# Revit family: DAC-H
name_source: partatom
category: Air Terminals
revit_build: Autodesk Revit MEP 2012 (Build: 20110309_2315(x64)
units: mm (PartAtom-declared; Revit-internal decimal feet)

## types (10) — shared parameters
Manufacturer = INNES
Max Flow = 0 CFM
Min Flow = 0 CFM
Máxima presión estática = 0.00 in-wg
Máxima velocidad de cuello = 0 FPM
Mínima presión estática = 0.00 in-wg
Mínima velocidad de cuello = 0 FPM
URL = http://www.innes.com.mx

## per-type parameters (varying)
| type | A | Ancho perfil medio | B | C | Cuello | Deflector | Largo frente | Largo perfil | Material | Medida req. | Máximo nivel de ruido (NC) | Perfil central | Soportes |
| DAC-I-01-3 | 3" | 1 31/32" | 5 3/4" | 4 11/16" |  | Yes | 146 7/8" | 143 15/16" |  | 144" |  | No | Yes |
| DAC-I-01-1 | 1" | 1 31/32" | 3 3/4" | 2 11/16" | Cuadrado | Yes | 26 7/8" | 23 15/16" | Aluminio | 24" | 32 | No | Yes |
| DAC-I-01-1 1/2 | 1 1/2" | 1 31/32" | 4 1/4" | 3 3/16" |  | Yes | 74 7/8" | 71 15/16" |  | 72" |  | No | Yes |
| DAC-I-01-2 | 2" | 1 31/32" | 4 3/4" | 3 11/16" |  | Yes | 50 7/8" | 47 15/16" |  | 48" |  | No | Yes |
| DAC-I-01-2 1/2 | 2 1/2" | 1 31/32" | 5 1/4" | 4 3/16" |  | Yes | 50 7/8" | 47 15/16" |  | 48" |  | No | Yes |
| DAC-I-02-1 | 3 3/8" | 1 3/8" | 6 1/8" | 5" |  | No | 26 7/8" | 23 15/16" |  | 24" |  | Yes | No |
| DAC-I-02-3 | 7 3/8" | 1 3/8" | 10 1/8" | 9" |  | No | 26 7/8" | 23 15/16" |  | 24" |  | Yes | No |
| DAC-I-02-1 1/2 | 4 3/8" | 1 3/8" | 7 1/8" | 6" |  | No | 50 7/8" | 47 15/16" |  | 48" |  | Yes | No |
| DAC-I-02-2 | 5 3/8" | 1 3/8" | 8 1/8" | 7" |  | No | 74 7/8" | 71 15/16" |  | 72" |  | Yes | No |
| DAC-I-02-2 1/2 | 6 3/8" | 1 3/8" | 9 1/8" | 8" |  | No | 50 7/8" | 47 15/16" |  | 48" |  | Yes | No |

## geometry (parser evidence)
native form markers: Sweep x1
no freeform markers — native parametric forms only
